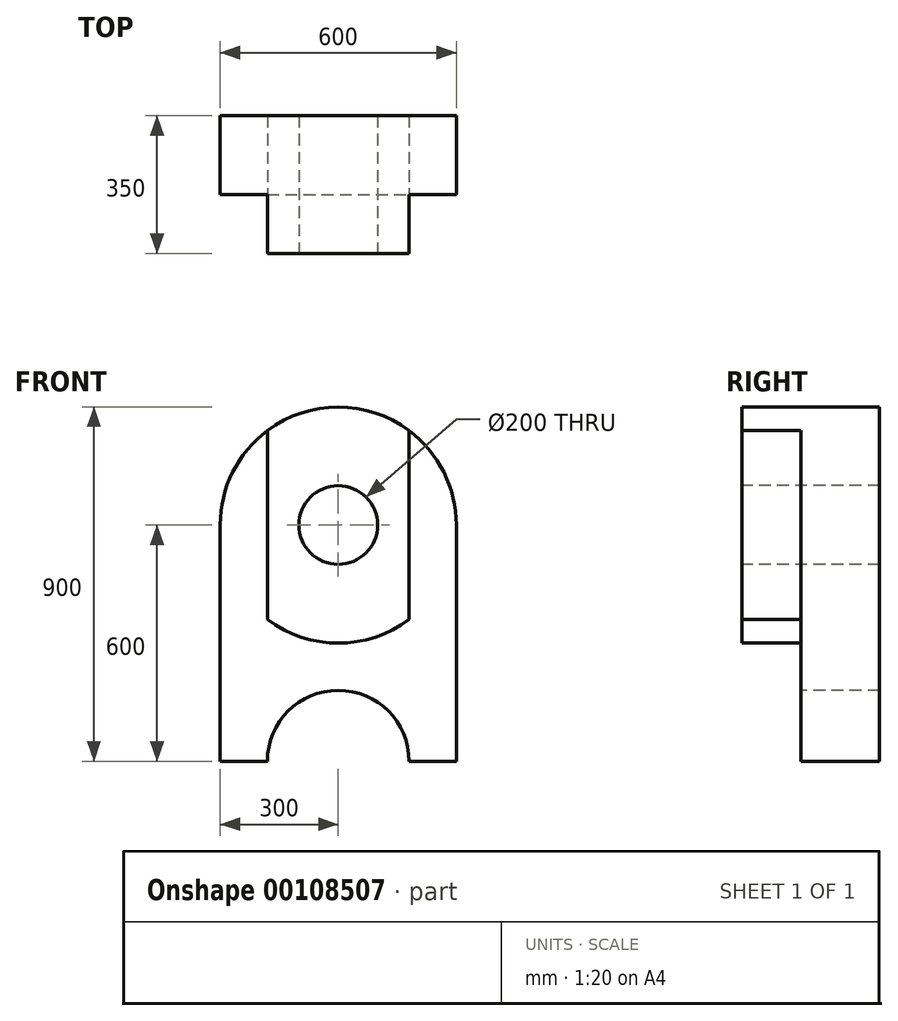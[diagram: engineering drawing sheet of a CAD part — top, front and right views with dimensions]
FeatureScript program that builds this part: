
annotation { "Feature Type Name" : "Feature", "Feature Type Description" : "" }
export const myFeature = defineFeature(function(context is Context, id is Id, definition is map)
    precondition{}
    {
        {
            var Q0;
            Q0=qCreatedBy(makeId("Front.planeOp"),FACE);
            var sketch = newSketch(context, id + "F0", { "sketchPlane" : qUnion([Q0])});
            skLineSegment(sketch, "E0.bottom", {"start": v(300, 300) * mm, "end": v(-300, 300) * mm});
            skLineSegment(sketch, "E0.top", {"start": v(300, -300) * mm, "end": v(-300, -300) * mm});
            skLineSegment(sketch, "E0.left", {"start": v(300, 300) * mm, "end": v(300, -300) * mm});
            skLineSegment(sketch, "E0.right", {"start": v(-300, 300) * mm, "end": v(-300, -300) * mm});
            skPoint(sketch, "E0.middle", {"position": v(0, 0) * mm});
            skSolve(sketch);
        }
        {
            var Q0;
            Q0 = qSketchRegion(id + "F0", true);
            extrude(context, id + "F1", {"entities" : qUnion([Q0]), "depth" : 200 * mm});
        }
        {
            var Q0;
            Q0=makeQuery(id+"F1.opExtrude","CAP_FACE",FACE,{"disambiguationData":[OSD([sQuery(id+"F0.wireOp",EDGE,"E0.bottom"),sQuery(id+"F0.wireOp",EDGE,"E0.top"),sQuery(id+"F0.wireOp",EDGE,"E0.left"),sQuery(id+"F0.wireOp",EDGE,"E0.right")])],"isStart":false});
            var sketch = newSketch(context, id + "F2", { "sketchPlane" : qUnion([Q0])});
            skCircle(sketch, "E1", {"center": v(0, -300) * mm, "radius": 180 * mm});
            skSolve(sketch);
        }
        {
            var Q0;
            Q0 = qSketchRegion(id + "F2", true);
            extrude(context, id + "F3", {"entities" : qUnion([Q0]), "operationType" : NewBodyOperationType.REMOVE, "endBound" : BoundingType.THROUGH_ALL, "oppositeDirection" : true, "depth" : 25 * mm});
        }
        {
            var Q0;
            Q0=makeQuery(id+"F1.opExtrude","CAP_FACE",FACE,{"disambiguationData":[OSD([sQuery(id+"F0.wireOp",EDGE,"E0.bottom"),sQuery(id+"F0.wireOp",EDGE,"E0.top"),sQuery(id+"F0.wireOp",EDGE,"E0.left"),sQuery(id+"F0.wireOp",EDGE,"E0.right")])],"isStart":false});
            var sketch = newSketch(context, id + "F4", { "sketchPlane" : qUnion([Q0])});
            skArc(sketch, "E2", {"start": v(300, 300) * mm, "mid": v(0, 600) * mm, "end": v(-300, 300) * mm});
            skLineSegment(sketch, "E3", {"start": v(-300, 300) * mm, "end": v(300, 300) * mm});
            skSolve(sketch);
        }
        {
            var Q0;
            Q0 = qSketchRegion(id + "F4", true);
            var Q1;
            Q1=makeQuery(id+"F4.imprint","IMPRINT",FACE,{"disambiguationData":[TD([[makeQuery(id+"F4.imprint","IMPRINT",EDGE,{"derivedFrom":sQuery(id+"F4.wireOp",EDGE,"E3")}),1.0]])]});
            extrude(context, id + "F5", {"entities" : qUnion([Q0, Q1]), "operationType" : NewBodyOperationType.ADD, "oppositeDirection" : true, "depth" : 200 * mm});
        }
        {
            var Q0;
            {var subQ0=sQuery(id+"F0.wireOp",EDGE,"E0.right");var subQ1=sQuery(id+"F0.wireOp",EDGE,"E0.left");var subQ2=sQuery(id+"F0.wireOp",EDGE,"E0.top");Q0=makeQuery(id+"F5.boolean.opBoolean","MERGE",FACE,{"derivedFrom":[makeQuery(id+"F1.opExtrude","CAP_FACE",FACE,{"disambiguationData":[OSD([sQuery(id+"F0.wireOp",EDGE,"E0.bottom"),subQ2,subQ1,subQ0])],"isStart":false}),makeQuery(id+"F5.opExtrude","CAP_FACE",FACE,{"disambiguationData":[OSD([subQ2,subQ1,subQ0,sQuery(id+"F2.wireOp",EDGE,"E1"),sQuery(id+"F4.wireOp",EDGE,"E2")])],"isStart":true})]});}
            var sketch = newSketch(context, id + "F6", { "sketchPlane" : qUnion([Q0])});
            skArc(sketch, "E4", {"start": v(-180, 60) * mm, "mid": v(0, 0) * mm, "end": v(180, 60) * mm});
            skLineSegment(sketch, "E5.left", {"start": v(180, 60) * mm, "end": v(180, 540) * mm});
            skLineSegment(sketch, "E5.right", {"start": v(-180, 60) * mm, "end": v(-180, 540) * mm});
            skArc(sketch, "E6.trimOffspring", {"start": v(180, 540) * mm, "mid": v(0, 600) * mm, "end": v(-180, 540) * mm});
            skSolve(sketch);
        }
        {
            var Q0;
            Q0 = qSketchRegion(id + "F6", true);
            extrude(context, id + "F7", {"entities" : qUnion([Q0]), "operationType" : NewBodyOperationType.ADD, "depth" : 150 * mm});
        }
        {
            var Q0;
            Q0=makeQuery(id+"F7.opExtrude","CAP_FACE",FACE,{"disambiguationData":[OSD([sQuery(id+"F6.wireOp",EDGE,"E4"),sQuery(id+"F6.wireOp",EDGE,"E5.left"),sQuery(id+"F6.wireOp",EDGE,"E5.right"),sQuery(id+"F6.wireOp",EDGE,"E6.trimOffspring")])],"isStart":false});
            var sketch = newSketch(context, id + "F8", { "sketchPlane" : qUnion([Q0])});
            skCircle(sketch, "E7", {"center": v(0, 300) * mm, "radius": 100 * mm});
            skSolve(sketch);
        }
        {
            var Q0;
            Q0 = qSketchRegion(id + "F8", true);
            extrude(context, id + "F9", {"entities" : qUnion([Q0]), "operationType" : NewBodyOperationType.REMOVE, "endBound" : BoundingType.THROUGH_ALL, "oppositeDirection" : true, "depth" : 25 * mm});
        }
    });
